# Revit family: VM-5806R_VM-5808R_Series
name_source: partatom
category: Pipe Accessories
revit_build: Autodesk Revit 2014 (Build: 20130308_1515(x64)
units: mm (PartAtom-declared; Revit-internal decimal feet)

## types (2) — shared parameters
Actuator Mount Height = 5.88 "
Assembly Code = D2090800
Bolt Size = 0.75 "
CW Connection = No
CWP (PSI) = 175.00 psi
Description = ANSI Class 125 Flanged Cam-centric rectangular plug valve.
HW Connection = No
Manufacturer = Zoeller
Material = Metal-Zoeller-Cast Iron
Model = VMC-5806R/BS
No. of Bolts = 8
Price = Prices may vary. Please consult Manufacturer Representative for most up-to-date price list.
Vent Connection = No
Waste Connection = No
Wrench = VM-3L_Series : 8L
zero-valued in all types: Default Elevation

## per-type parameters (varying)
| type | Actuator Mount Base Diameter | Actuator Mount Diameter | Center to Bottom | Center to Top | Flange Diameter | Flange Thickness | Height | Length | Nominal Length | Valve Size | Width |
| 6030-0087 - 6" | 2.903 " | 1.451 " | 7.06 " | 12.31 " | 11 " | 0.75 " | 19.37 " | 10.5 " | 1.088 " | 6 " | 10.5 " |
| 6030-0088 - 8" | 2.992 " | 1.496 " | 8.75 " | 13.881 " | 13.5 " | 0.88 " | 22.631 " | 11.5 " | 1.122 " | 8 " | 11.5 " |

## geometry (parser evidence)
native form markers: Sweep x4
no freeform markers — native parametric forms only
